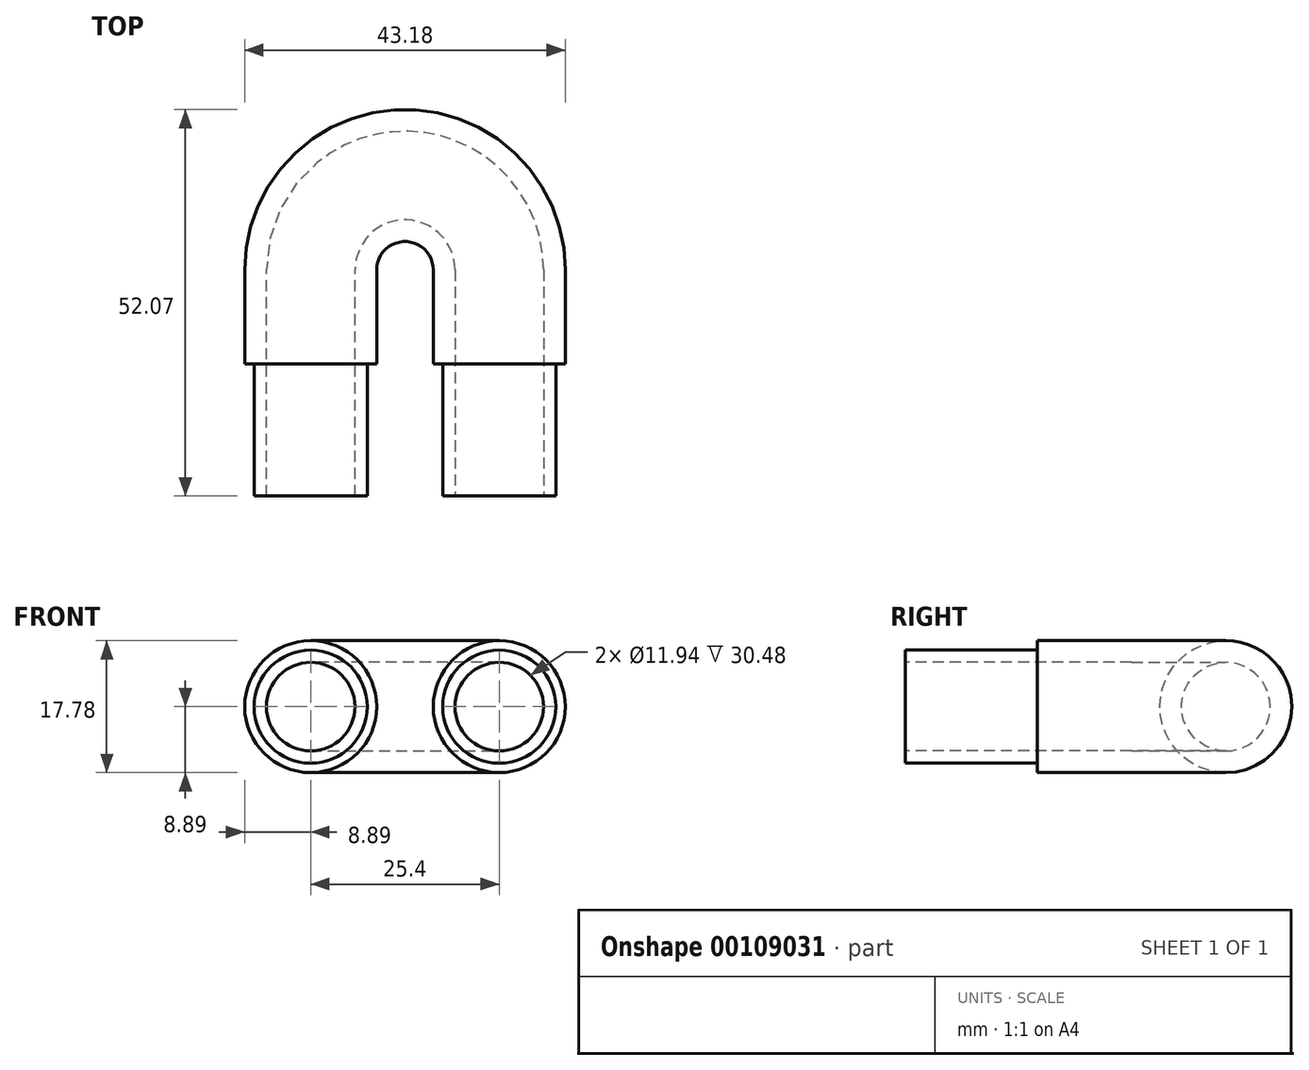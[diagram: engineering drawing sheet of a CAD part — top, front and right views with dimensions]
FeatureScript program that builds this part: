
annotation { "Feature Type Name" : "Feature", "Feature Type Description" : "" }
export const myFeature = defineFeature(function(context is Context, id is Id, definition is map)
    precondition{}
    {
        {
            var Q0;
            Q0=qCreatedBy(makeId("Front.planeOp"),FACE);
            var sketch = newSketch(context, id + "F0", { "sketchPlane" : qUnion([Q0])});
            skCircle(sketch, "E0", {"center": v(0, 0) * mm, "radius": 5.97 * mm});
            skCircle(sketch, "E1", {"center": v(0, 0) * mm, "radius": 8.9 * mm});
            skSolve(sketch);
        }
        {
            var Q0;
            Q0=qCreatedBy(makeId("Top.planeOp"),FACE);
            var sketch = newSketch(context, id + "F1", { "sketchPlane" : qUnion([Q0])});
            skLineSegment(sketch, "E2", {"start": v(0, 0) * mm, "end": v(0, 12.7) * mm});
            skArc(sketch, "E3", {"start": v(0, 12.7) * mm, "mid": v(12.7, 25.4) * mm, "end": v(25.4, 12.7) * mm});
            skLineSegment(sketch, "E4", {"start": v(25.4, 12.7) * mm, "end": v(25.4, 0) * mm});
            skLineSegment(sketch, "E5", {"start": v(12.7, 25.4) * mm, "end": v(12.7, 0) * mm});
            skSolve(sketch);
        }
        {
            var Q0;
            Q0=makeQuery(id+"F0.imprint","IMPRINT",FACE,{"disambiguationData":[TD([[makeQuery(id+"F0.imprint","IMPRINT",EDGE,{"derivedFrom":sQuery(id+"F0.wireOp",EDGE,"E0")}),-1.0]])]});
            var Q1;
            Q1=sQuery(id+"F1.wireOp",EDGE,"E2");
            var Q2;
            Q2=sQuery(id+"F1.wireOp",EDGE,"E3");
            var Q3;
            Q3=sQuery(id+"F1.wireOp",EDGE,"E4");
            sweep(context, id + "F2", {"profiles" : qUnion([Q0]), "path" : qUnion([Q1, Q2, Q3])});
        }
        {
            var Q0;
            Q0=makeQuery(id+"F2.opSweep","CAP_FACE",FACE,{"disambiguationData":[OSD([sQuery(id+"F0.wireOp",EDGE,"E0"),sQuery(id+"F0.wireOp",EDGE,"E1"),sQuery(id+"F1.wireOp",VERTEX,"E2.start")])],"isStart":true});
            var sketch = newSketch(context, id + "F3", { "sketchPlane" : qUnion([Q0])});
            skCircle(sketch, "E6", {"center": v(0, 0) * mm, "radius": 7.62 * mm});
            skSolve(sketch);
        }
        {
            var Q0;
            Q0=makeQuery(id+"F2.opSweep","CAP_FACE",FACE,{"disambiguationData":[OSD([sQuery(id+"F0.wireOp",EDGE,"E0"),sQuery(id+"F0.wireOp",EDGE,"E1"),sQuery(id+"F1.wireOp",VERTEX,"E4.end")])],"isStart":false});
            var sketch = newSketch(context, id + "F4", { "sketchPlane" : qUnion([Q0])});
            skCircle(sketch, "E7", {"center": v(25.4, 0) * mm, "radius": 7.62 * mm});
            skSolve(sketch);
        }
        {
            var Q0;
            Q0=makeQuery(id+"F3.imprint","IMPRINT",FACE,{"disambiguationData":[TD([[makeQuery(id+"F3.imprint","IMPRINT",EDGE,{"derivedFrom":sQuery(id+"F3.wireOp",EDGE,"E6")}),1.0]])]});
            var Q1;
            Q1=makeQuery(id+"F4.imprint","IMPRINT",FACE,{"disambiguationData":[TD([[makeQuery(id+"F4.imprint","IMPRINT",EDGE,{"derivedFrom":sQuery(id+"F4.wireOp",EDGE,"E7")}),1.0]])]});
            extrude(context, id + "F5", {"entities" : qUnion([Q0, Q1]), "operationType" : NewBodyOperationType.ADD, "depth" : 17.78 * mm});
        }
    });
